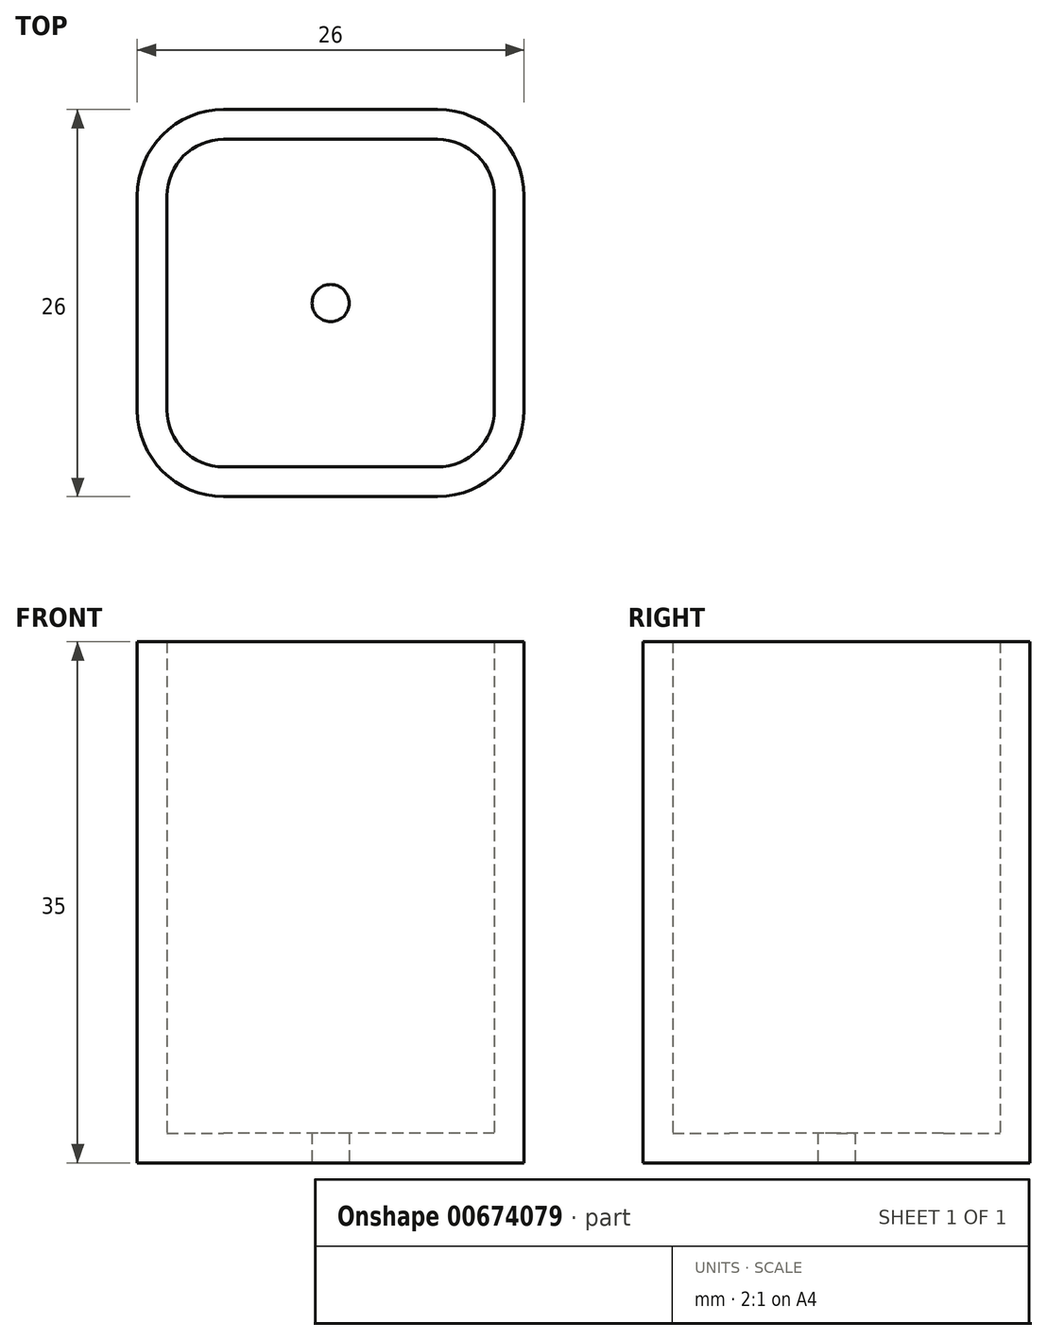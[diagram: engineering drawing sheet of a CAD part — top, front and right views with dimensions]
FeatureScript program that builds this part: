
annotation { "Feature Type Name" : "Feature", "Feature Type Description" : "" }
export const myFeature = defineFeature(function(context is Context, id is Id, definition is map)
    precondition{}
    {
        {
            var Q0;
            Q0=qCreatedBy(makeId("Top.planeOp"),FACE);
            var sketch = newSketch(context, id + "F0", { "sketchPlane" : qUnion([Q0])});
            skCircle(sketch, "E0.cCircle", {"center": v(0, 0) * mm, "radius": 11 * mm, "construction": true});
            skLineSegment(sketch, "E0.0", {"start": v(-7.2, 11) * mm, "end": v(7.2, 11) * mm});
            skLineSegment(sketch, "E0.1", {"start": v(11, 7.2) * mm, "end": v(11, -7.2) * mm});
            skLineSegment(sketch, "E0.2", {"start": v(7.2, -11) * mm, "end": v(-7.2, -11) * mm});
            skLineSegment(sketch, "E0.3", {"start": v(-11, -7.2) * mm, "end": v(-11, 7.2) * mm});
            skPoint(sketch, "E0.0.midPoint", {"position": v(0, 11) * mm});
            skPoint(sketch, "E1.visualSharp", {"position": v(-11, 11) * mm});
            skArc(sketch, "E1.filletArc", {"start": v(-7.2, 11) * mm, "mid": v(-9.88, 9.88) * mm, "end": v(-11, 7.2) * mm});
            skPoint(sketch, "E2.visualSharp", {"position": v(11, 11) * mm});
            skArc(sketch, "E2.filletArc", {"start": v(11, 7.2) * mm, "mid": v(9.88, 9.88) * mm, "end": v(7.2, 11) * mm});
            skPoint(sketch, "E3.visualSharp", {"position": v(11, -11) * mm});
            skArc(sketch, "E3.filletArc", {"start": v(7.2, -11) * mm, "mid": v(9.88, -9.88) * mm, "end": v(11, -7.2) * mm});
            skPoint(sketch, "E4.visualSharp", {"position": v(-11, -11) * mm});
            skArc(sketch, "E4.filletArc", {"start": v(-11, -7.2) * mm, "mid": v(-9.88, -9.88) * mm, "end": v(-7.2, -11) * mm});
            skLineSegment(sketch, "E5.0", {"start": v(13, 7.2) * mm, "end": v(13, -7.2) * mm});
            skArc(sketch, "E5.1", {"start": v(7.2, -13) * mm, "mid": v(11.3, -11.3) * mm, "end": v(13, -7.2) * mm});
            skArc(sketch, "E5.2", {"start": v(13, 7.2) * mm, "mid": v(11.3, 11.3) * mm, "end": v(7.2, 13) * mm});
            skLineSegment(sketch, "E5.3", {"start": v(7.2, -13) * mm, "end": v(-7.2, -13) * mm});
            skLineSegment(sketch, "E5.4", {"start": v(-7.2, 13) * mm, "end": v(7.2, 13) * mm});
            skArc(sketch, "E5.5", {"start": v(-7.2, 13) * mm, "mid": v(-11.3, 11.3) * mm, "end": v(-13, 7.2) * mm});
            skLineSegment(sketch, "E5.6", {"start": v(-13, -7.2) * mm, "end": v(-13, 7.2) * mm});
            skArc(sketch, "E5.7", {"start": v(-13, -7.2) * mm, "mid": v(-11.3, -11.3) * mm, "end": v(-7.2, -13) * mm});
            skSolve(sketch);
        }
        {
            var Q0;
            Q0=makeQuery(id+"F0.imprint","IMPRINT",FACE,{"disambiguationData":[TD([[makeQuery(id+"F0.imprint","IMPRINT",EDGE,{"derivedFrom":sQuery(id+"F0.wireOp",EDGE,"E0.0")}),1.0]])]});
            extrude(context, id + "F1", {"entities" : qUnion([Q0]), "depth" : 35 * mm, "offsetDistance" : 25.4 * mm});
        }
        {
            var Q0;
            Q0=makeQuery(id+"F0.imprint","IMPRINT",FACE,{"disambiguationData":[TD([[makeQuery(id+"F0.imprint","IMPRINT",EDGE,{"derivedFrom":sQuery(id+"F0.wireOp",EDGE,"E0.0")}),-1.0]])]});
            extrude(context, id + "F2", {"entities" : qUnion([Q0]), "operationType" : NewBodyOperationType.ADD, "depth" : 2 * mm, "offsetDistance" : 25.4 * mm});
        }
        {
            var Q0;
            Q0=sQuery(id+"F0.wireOp",VERTEX,"E0.cCircle.center");
            var Q1;
            Q1=makeQuery(id+"F1.opExtrude","SWEPT_BODY",BODY,{"disambiguationData":[OSD([sQuery(id+"F0.wireOp",EDGE,"E0.0"),sQuery(id+"F0.wireOp",EDGE,"E0.1"),sQuery(id+"F0.wireOp",EDGE,"E0.2"),sQuery(id+"F0.wireOp",EDGE,"E0.3"),sQuery(id+"F0.wireOp",EDGE,"E1.filletArc"),sQuery(id+"F0.wireOp",EDGE,"E2.filletArc"),sQuery(id+"F0.wireOp",EDGE,"E3.filletArc"),sQuery(id+"F0.wireOp",EDGE,"E4.filletArc"),sQuery(id+"F0.wireOp",EDGE,"E5.0"),sQuery(id+"F0.wireOp",EDGE,"E5.1"),sQuery(id+"F0.wireOp",EDGE,"E5.2"),sQuery(id+"F0.wireOp",EDGE,"E5.3"),sQuery(id+"F0.wireOp",EDGE,"E5.4"),sQuery(id+"F0.wireOp",EDGE,"E5.5"),sQuery(id+"F0.wireOp",EDGE,"E5.6"),sQuery(id+"F0.wireOp",EDGE,"E5.7")])]});
            hole(context, id + "F3", {"style" : HoleStyle.SIMPLE, "endStyle" : HoleEndStyle.THROUGH, "oppositeDirection" : true, "holeDiameter" : 2.5 * mm, "majorDiameter" : 6.35 * mm, "isTappedThrough" : true, "tappedDepth" : 12.7 * mm, "tapClearance" : 3, "locations" : qUnion([Q0]), "scope" : qUnion([Q1])});
        }
    });
